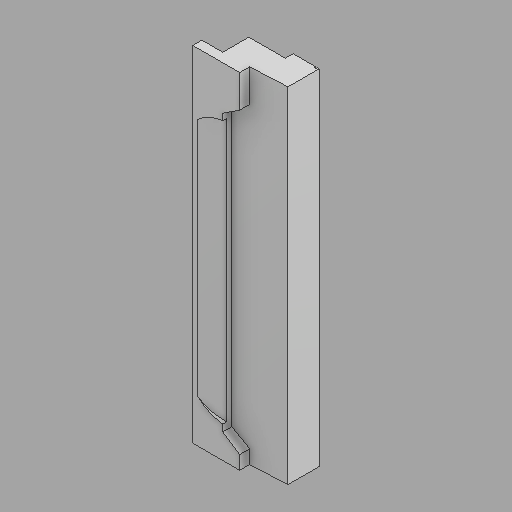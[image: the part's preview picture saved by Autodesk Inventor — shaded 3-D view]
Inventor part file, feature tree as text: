
AUTODESK INVENTOR PART (.ipt)
format: ipt  version: 2023 (Build 270158030, 158C)  size: 135,680 bytes
history: native  units: in
note: dims shown in document units (in); Inventor stores cm internally (conversion verified against a paired STEP export)
features: extrude x1, sketch x1, other x1
ambient origin geometry x8: Origin, YZ Plane, XZ Plane, XY Plane, X Axis, Y Axis, Z Axis, Center Point
bodies: Solid1 (feature_tree)
feature tree (3):
  extrude  "Extrusion1"  [1 undecoded]
  sketch  "Sketch2"  dims[d0=1.0in d1=0.0in]
  other  "Screen sill H - 1"
note: 1 required parameter value undecoded (feature->parameter linkage not recoverable at this tier; creation-order binding heuristic only, values carry confidence <= 0.55)
